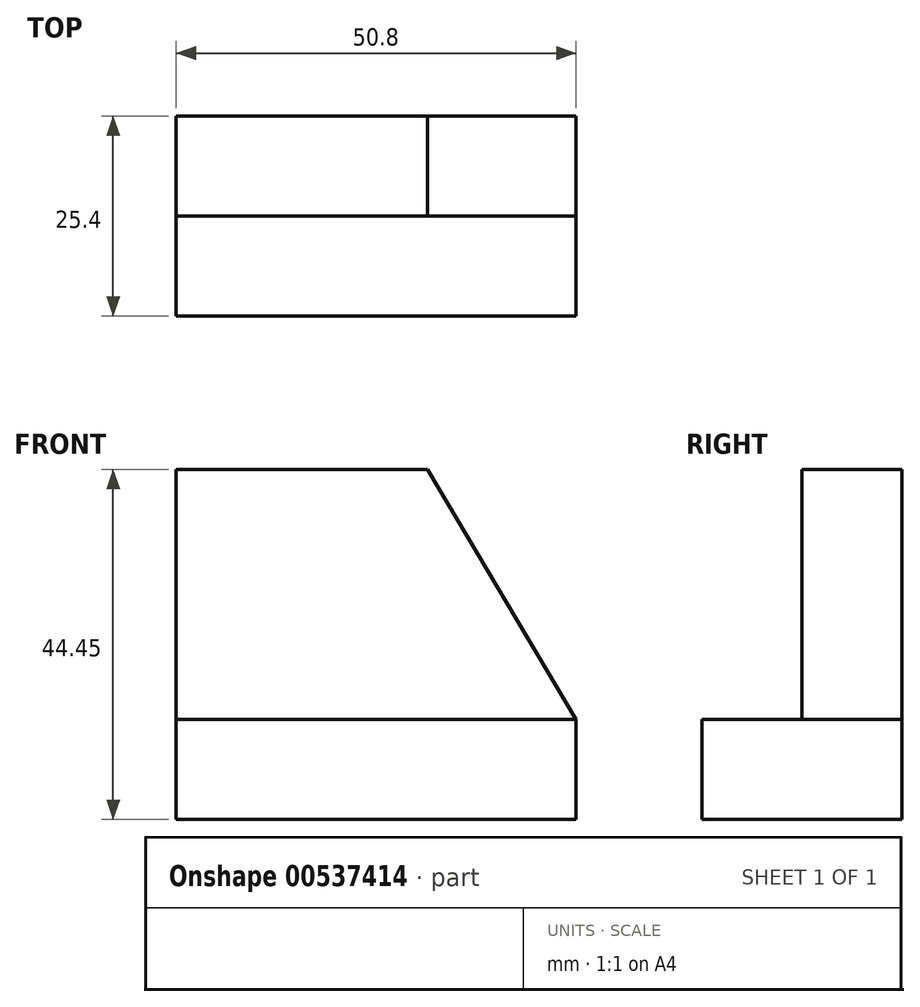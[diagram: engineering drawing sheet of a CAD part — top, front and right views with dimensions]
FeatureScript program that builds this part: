
annotation { "Feature Type Name" : "Feature", "Feature Type Description" : "" }
export const myFeature = defineFeature(function(context is Context, id is Id, definition is map)
    precondition{}
    {
        {
            var Q0;
            Q0=qCreatedBy(makeId("Front.planeOp"),FACE);
            var sketch = newSketch(context, id + "F0", { "sketchPlane" : qUnion([Q0])});
            skLineSegment(sketch, "E0", {"start": v(0, 0) * mm, "end": v(0, 44.45) * mm});
            skLineSegment(sketch, "E1", {"start": v(0, 44.45) * mm, "end": v(31.95, 44.45) * mm});
            skLineSegment(sketch, "E2", {"start": v(31.95, 44.45) * mm, "end": v(50.8, 12.7) * mm});
            skLineSegment(sketch, "E3", {"start": v(50.8, 12.7) * mm, "end": v(50.8, 0) * mm});
            skLineSegment(sketch, "E4", {"start": v(50.8, 0) * mm, "end": v(0, 0) * mm});
            skSolve(sketch);
        }
        {
            var Q0;
            Q0=makeQuery(id+"F0.imprint","IMPRINT",FACE,{"disambiguationData":[TD([[makeQuery(id+"F0.imprint","IMPRINT",EDGE,{"derivedFrom":sQuery(id+"F0.wireOp",EDGE,"E0")}),-1.0]])]});
            extrude(context, id + "F1", {"entities" : qUnion([Q0]), "depth" : 12.7 * mm, "offsetDistance" : 25.4 * mm});
        }
        {
            var Q0;
            Q0=makeQuery(id+"F1.opExtrude","CAP_FACE",FACE,{"disambiguationData":[OSD([sQuery(id+"F0.wireOp",EDGE,"E0"),sQuery(id+"F0.wireOp",EDGE,"E1"),sQuery(id+"F0.wireOp",EDGE,"E2"),sQuery(id+"F0.wireOp",EDGE,"E3"),sQuery(id+"F0.wireOp",EDGE,"E4")])],"isStart":false});
            var sketch = newSketch(context, id + "F2", { "sketchPlane" : qUnion([Q0])});
            skLineSegment(sketch, "E5", {"start": v(50.8, 12.7) * mm, "end": v(0, 12.7) * mm});
            skLineSegment(sketch, "E6", {"start": v(0, 12.7) * mm, "end": v(0, 0) * mm});
            skLineSegment(sketch, "E7", {"start": v(0, 0) * mm, "end": v(50.8, 0) * mm});
            skLineSegment(sketch, "E8", {"start": v(50.8, 0) * mm, "end": v(50.8, 12.7) * mm});
            skSolve(sketch);
        }
        {
            var Q0;
            Q0=makeQuery(id+"F2.imprint","IMPRINT",FACE,{"disambiguationData":[TD([[makeQuery(id+"F2.imprint","IMPRINT",EDGE,{"derivedFrom":sQuery(id+"F2.wireOp",EDGE,"E5")}),1.0]])]});
            extrude(context, id + "F3", {"entities" : qUnion([Q0]), "operationType" : NewBodyOperationType.ADD, "depth" : 12.7 * mm, "offsetDistance" : 25.4 * mm});
        }
    });
